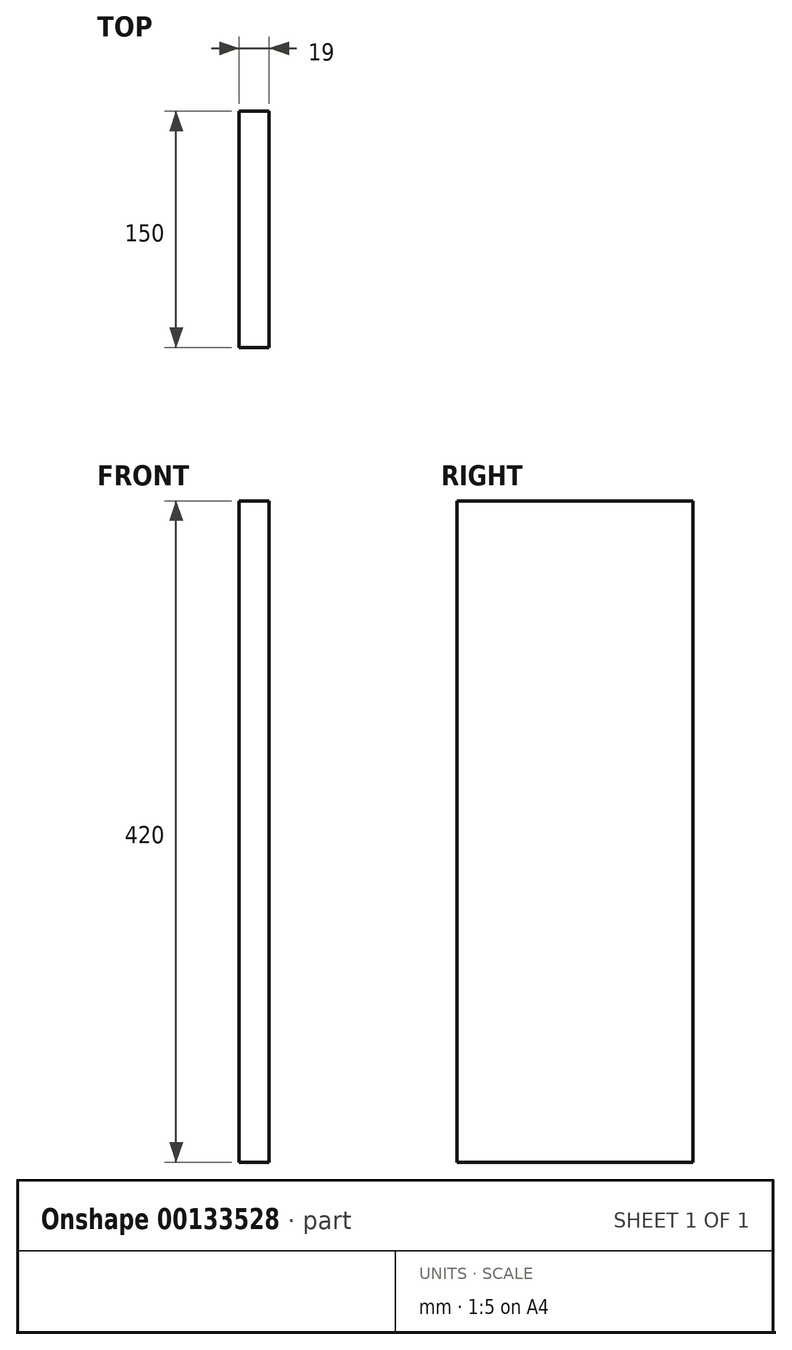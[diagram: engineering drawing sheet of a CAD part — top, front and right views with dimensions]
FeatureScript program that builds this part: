
annotation { "Feature Type Name" : "Feature", "Feature Type Description" : "" }
export const myFeature = defineFeature(function(context is Context, id is Id, definition is map)
    precondition{}
    {
        {
            var Q0;
            Q0=qCreatedBy(makeId("Right.planeOp"),FACE);
            var sketch = newSketch(context, id + "F0", { "sketchPlane" : qUnion([Q0])});
            skLineSegment(sketch, "E0", {"start": v(0, 420) * mm, "end": v(-150, 420) * mm});
            skLineSegment(sketch, "E1", {"start": v(-150, 420) * mm, "end": v(-150, 0) * mm});
            skLineSegment(sketch, "E2", {"start": v(-150, 0) * mm, "end": v(0, 0) * mm});
            skLineSegment(sketch, "E3", {"start": v(0, 0) * mm, "end": v(0, 420) * mm});
            skSolve(sketch);
        }
        {
            var Q0;
            Q0=makeQuery(id+"F0.imprint","IMPRINT",FACE,{"disambiguationData":[TD([[makeQuery(id+"F0.imprint","IMPRINT",EDGE,{"derivedFrom":sQuery(id+"F0.wireOp",EDGE,"E0")}),1.0]])]});
            extrude(context, id + "F1", {"entities" : qUnion([Q0]), "depth" : 19 * mm});
        }
    });
